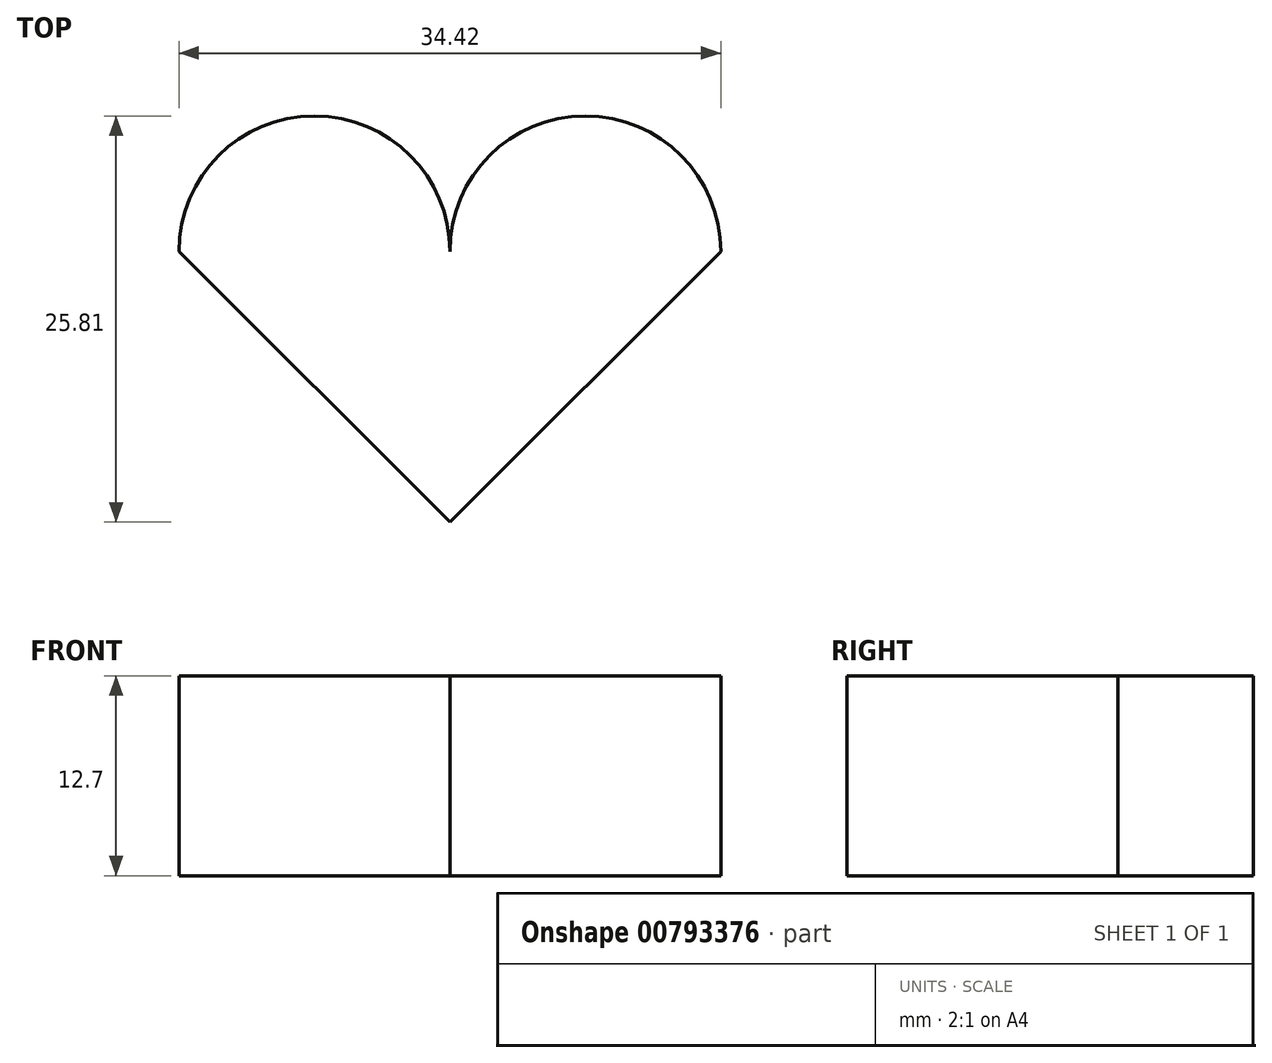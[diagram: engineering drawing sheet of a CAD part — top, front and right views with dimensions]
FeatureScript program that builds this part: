
annotation { "Feature Type Name" : "Feature", "Feature Type Description" : "" }
export const myFeature = defineFeature(function(context is Context, id is Id, definition is map)
    precondition{}
    {
        {
            var Q0;
            Q0=qCreatedBy(makeId("Top.planeOp"),FACE);
            var sketch = newSketch(context, id + "F0", { "sketchPlane" : qUnion([Q0])});
            skLineSegment(sketch, "E0", {"start": v(0, 0) * mm, "end": v(0, 17.2) * mm});
            skCircle(sketch, "E1", {"center": v(0, 17.2) * mm, "radius": 17.2 * mm});
            skLineSegment(sketch, "E2", {"start": v(-17.2, 17.2) * mm, "end": v(0, 0) * mm});
            skLineSegment(sketch, "E3", {"start": v(17.2, 17.2) * mm, "end": v(0, 0) * mm});
            skLineSegment(sketch, "E4", {"start": v(-17.2, 17.2) * mm, "end": v(0, 17.2) * mm});
            skLineSegment(sketch, "E5", {"start": v(0, 17.2) * mm, "end": v(17.2, 17.2) * mm});
            skCircle(sketch, "E6", {"center": v(-8.6, 17.2) * mm, "radius": 8.6 * mm});
            skCircle(sketch, "E7", {"center": v(8.6, 17.2) * mm, "radius": 8.6 * mm});
            skSolve(sketch);
        }
        {
            var Q0;
            {var subQ0=sQuery(id+"F0.wireOp",EDGE,"E4");Q0=makeQuery(id+"F0.imprint","IMPRINT",FACE,{"disambiguationData":[TD([[makeQuery(id+"F0.imprint","IMPRINT",EDGE,{"derivedFrom":subQ0}),1.0]])]});}
            var Q1;
            {var subQ1=sQuery(id+"F0.wireOp",EDGE,"E4");Q1=makeQuery(id+"F0.imprint","IMPRINT",FACE,{"disambiguationData":[TD([[makeQuery(id+"F0.imprint","IMPRINT",EDGE,{"derivedFrom":subQ1}),-1.0]])]});}
            var Q2;
            {var subQ0=sQuery(id+"F0.wireOp",EDGE,"E0");Q2=makeQuery(id+"F0.imprint","IMPRINT",FACE,{"disambiguationData":[TD([[makeQuery(id+"F0.imprint","IMPRINT",EDGE,{"derivedFrom":subQ0}),1.0]])]});}
            var Q3;
            {var subQ0=sQuery(id+"F0.wireOp",EDGE,"E0");Q3=makeQuery(id+"F0.imprint","IMPRINT",FACE,{"disambiguationData":[TD([[makeQuery(id+"F0.imprint","IMPRINT",EDGE,{"derivedFrom":subQ0}),-1.0]])]});}
            var Q4;
            {var subQ1=sQuery(id+"F0.wireOp",EDGE,"E5");Q4=makeQuery(id+"F0.imprint","IMPRINT",FACE,{"disambiguationData":[TD([[makeQuery(id+"F0.imprint","IMPRINT",EDGE,{"derivedFrom":subQ1}),-1.0]])]});}
            var Q5;
            {var subQ0=sQuery(id+"F0.wireOp",EDGE,"E5");Q5=makeQuery(id+"F0.imprint","IMPRINT",FACE,{"disambiguationData":[TD([[makeQuery(id+"F0.imprint","IMPRINT",EDGE,{"derivedFrom":subQ0}),1.0]])]});}
            extrude(context, id + "F1", {"entities" : qUnion([Q0, Q1, Q2, Q3, Q4, Q5]), "depth" : 12.7 * mm, "offsetDistance" : 25.4 * mm});
        }
    });
